# Revit family: highbay_11_51hl61d24hca
name_source: partatom
category: Lighting Fixtures
units: mm (PartAtom-declared; Revit-internal decimal feet)

## family parameters
Cut with Voids When Loaded = No
Host = Face
Light Source = No
Part Type = Normal
Room Calculation Point = No
Round Connector Dimension = Use Diameter
Shared = No

## types (1)
- --- (1 x LED, 19570 lm, 111.2 W, 4000K)
    Apparent Load = 111 VA
    CIE Flux Codes = 88 95 99 100 99
    Color Rendering = 80
    Color Temperature = 4000K
    Default Elevation = 1800 mm
    Description = Highbay 11, LED high bay luminaire, primary light control with lens, of PMMA, light emission: direct distribution, primary light characteristic: symmetric, installation type: surface-mounted, suspended mounting, for 2x 2 x LED rated luminous flux: 19.570 lm, light colour: 840, colour temperature: 4000K, control gear: ECG DALI, with terminal, 5-pole, max. 2.5mm², mains connection: 230..240V, AC, 50/60Hz, rated input power: 111W, LED unit, of diecast aluminium, coated, metallic grey (RAL 9006), length: 940 mm, width: 500 mm, height: 65mm, housing, of diecast aluminium, coated, metallic grey (RAL 9006), protection rating (complete): IP65, insulation class (complete): insulation class I (protective earthing), certification: CE, ENEC, VDE, protection symbol: D, impact resistance: IK08 with glass or PC cover, permissible ambient temperature for indoor applications: -35..+70°C, corresponds to IFS (International Featured Standards) requirements for safety and quality in the food industry, reducing of maximum allowable ambient temperature of 5°C with ceiling mounting, packaging unit: 1 piece
    Height = 95 mm
    Lamp = 1 x LED
    Lamp Light Flux = 19570 lm
    Lamp Power = 111.2 W
    Lamp count = 1
    Length = 939 mm
    Luminous efficacy = 176 lm/W
    Manufacturer = Siteco
    ModVariant = No
    Model = 51HL61D24HCA
    Mounting Place = Ceiling
    Mounting Type = Pendant
    Number of Poles = 1
    OnlyDefault = Yes
    Power Factor = 1
    Product Name = Highbay 11
    Product group = LED high bay luminaire
    ProductGroupID = 903
    Protection Class = Protection class I
    Protection Degree = IP 65
    RLX_Detail_Level = 1
    RlxData = <blob elided: 76901 chars, md5=08e11918>
    Socket = socket
    Standby Power = 0 W
    System Light Flux = 19570 lm
    System Power = 111 W
    Type Comments = factory setting: luminous flux: 100 % | dim-lin: 254 | 315 mA
    Type Image = l_1003428.jpg
    URL = http://relux.com
    VarID = @adj_140973
    Voltage = 0 V
    Weight = 0.00 kg
    Width = 501 mm

## geometry (parser evidence)
native form markers: Sweep x12
no freeform markers — native parametric forms only
